SOLIDWORKS PART (.sldprt)
format: sldprt  version: not decoded by parser v0  size: 137,728 bytes
history: native  units: mm
features: sketch x11, cut_extrude x9, fillet x3, extrude x2 + 2 further entries (+8 scaffold rows collapsed; 3 parser-record rows omitted)
feature tree (38):
  scaffold x8  (default folders/planes/origin — collapsed)
  parser-record x3  (decoder bookkeeping rows leaked as tree rows — omitted from the tree; the rows remain in map.json)
  "ID2"
  "ID3"
  sketch  "Sketch1"  dims[D1=5.842mm D2=18.288mm]
  extrude  "Base-Extrude"  Depth=42.926mm
  sketch  "Sketch2"  dims[D1=12.7mm]
  extrude  "Boss-Extrude1"  [1 undecoded]
  sketch  "Sketch3"  dims[D1=5.08mm]
  cut_extrude  "Cut-Extrude1"  [1 undecoded]
  sketch  "Sketch4"  dims[c1.D1=8.89mm c1.D2=8.89mm c1.D3=8.89mm c2.D2=5.588mm c2.D3=5.588mm]
  cut_extrude  "Cut-Extrude2"  Depth=2.54mm
  sketch  "Sketch5"  dims[c1.D1=8.89mm c1.D2=8.89mm c2.D1=5.588mm c2.D2=5.588mm]
  cut_extrude  "Cut-Extrude4"  Depth=2.54mm
  sketch  "Sketch6"  dims[D1=5.0038mm]
  cut_extrude  "Cut-Extrude5"  [1 undecoded]
  sketch  "Sketch7"  dims[D1=5.0038mm]
  cut_extrude  "Cut-Extrude6"  [1 undecoded]
  sketch  "Sketch9"  dims[D1=10.922mm D2=10.922mm]
  cut_extrude  "Cut-Extrude7"  [1 undecoded]
  fillet  "Fillet1"  Radius=1.5748mm
  fillet  "Fillet3"  Radius=3.175mm
  fillet  "Fillet4"  Radius=3.175mm
  sketch  "Sketch10"  dims[D1=8.3566mm]
  cut_extrude  "Cut-Extrude8"  Depth=5.08mm
  sketch  "Sketch11"  dims[D1=~7.286263mm]
  cut_extrude  "Cut-Extrude9"  Depth=5.08mm
  sketch  "Sketch12"  dims[D1=0.7874mm]
  cut_extrude  "Cut-Extrude11"  [1 undecoded]
decode coverage: 19 of 25 modeling features carry decoded parameters; 2 rows unclassified (native names shown)
note: ~ marks probable driven/reference dimensions
note: 6 parameter values undecoded
summary: no parameter record found for 6 features
note: suppression state not decoded; provenance and decode notes live in map.json
